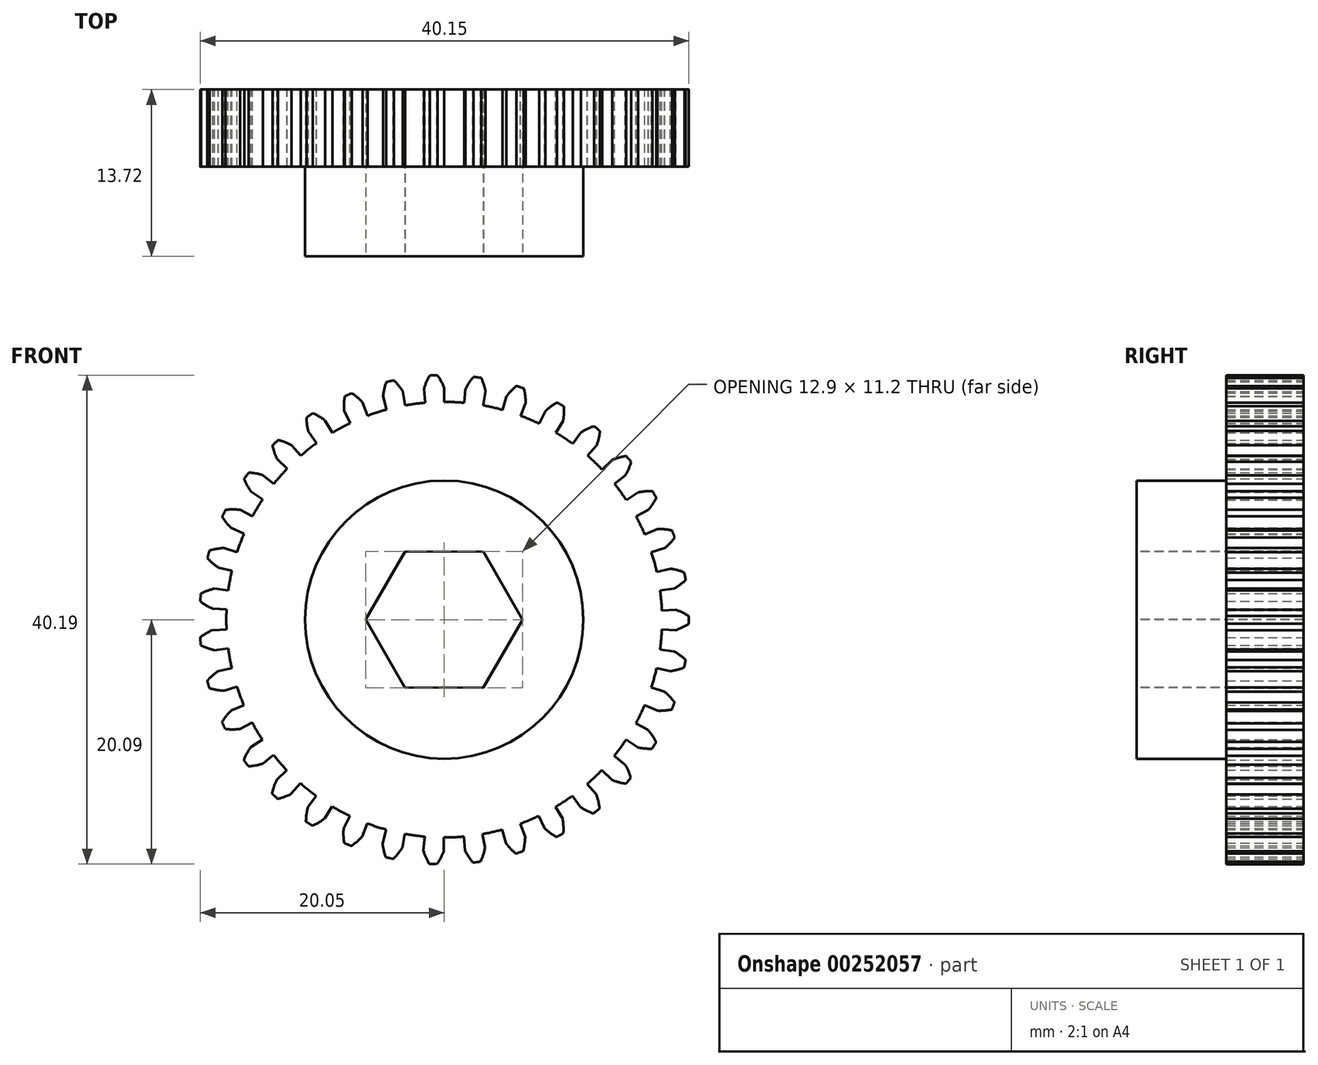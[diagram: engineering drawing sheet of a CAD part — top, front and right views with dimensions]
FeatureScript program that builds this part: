
annotation { "Feature Type Name" : "Feature", "Feature Type Description" : "" }
export const myFeature = defineFeature(function(context is Context, id is Id, definition is map)
    precondition{}
    {
        {
            var Q0;
            Q0=qCreatedBy(makeId("Front.planeOp"),FACE);
            var sketch = newSketch(context, id + "F0", { "sketchPlane" : qUnion([Q0])});
            skArc(sketch, "E0", {"start": v(-0.56, 20.1) * mm, "mid": v(-0.72, 20.1) * mm, "end": v(-0.88, 20.08) * mm});
            skLineSegment(sketch, "E1", {"start": v(0, 17.9) * mm, "end": v(0, 19.05) * mm});
            skArc(sketch, "E2", {"start": v(-1.56, 17.83) * mm, "mid": v(-2.38, 17.74) * mm, "end": v(-3.2, 17.61) * mm});
            skArc(sketch, "E3.trimOffspring", {"start": v(0, 19.05) * mm, "mid": v(-0.25, 19.6) * mm, "end": v(-0.56, 20.1) * mm});
            skPoint(sketch, "E4.orphan", {"position": v(0, 32.14) * mm});
            skPoint(sketch, "E5.orphan", {"position": v(-2.81, 32.14) * mm});
            skArc(sketch, "E6.MirrorCS", {"start": v(-1.2, 20.07) * mm, "mid": v(-1.03, 20.08) * mm, "end": v(-0.88, 20.08) * mm});
            skArc(sketch, "E7.MirrorCS", {"start": v(-1.66, 18.98) * mm, "mid": v(-1.46, 19.54) * mm, "end": v(-1.2, 20.07) * mm});
            skLineSegment(sketch, "E8.MirrorCS", {"start": v(-1.56, 17.83) * mm, "end": v(-1.66, 18.98) * mm});
            skPoint(sketch, "E9.orphan", {"position": v(-1.4, 32.14) * mm});
            skArc(sketch, "E10.1.0", {"start": v(-5.02, 18.38) * mm, "mid": v(-4.93, 18.96) * mm, "end": v(-4.76, 19.53) * mm});
            skArc(sketch, "E10.1.1", {"start": v(-4.76, 19.53) * mm, "mid": v(-4.6, 19.57) * mm, "end": v(-4.45, 19.6) * mm});
            skArc(sketch, "E10.1.2", {"start": v(-4.14, 19.67) * mm, "mid": v(-4.3, 19.64) * mm, "end": v(-4.45, 19.6) * mm});
            skArc(sketch, "E10.1.3", {"start": v(-3.4, 18.74) * mm, "mid": v(-3.74, 19.23) * mm, "end": v(-4.14, 19.67) * mm});
            skLineSegment(sketch, "E10.1.4", {"start": v(-3.2, 17.61) * mm, "end": v(-3.4, 18.74) * mm});
            skLineSegment(sketch, "E10.1.5", {"start": v(-4.72, 17.27) * mm, "end": v(-5.02, 18.38) * mm});
            skArc(sketch, "E10.2.0", {"start": v(-8.22, 17.18) * mm, "mid": v(-8.23, 17.78) * mm, "end": v(-8.17, 18.37) * mm});
            skArc(sketch, "E10.2.1", {"start": v(-8.17, 18.37) * mm, "mid": v(-8.02, 18.43) * mm, "end": v(-7.88, 18.5) * mm});
            skArc(sketch, "E10.2.2", {"start": v(-7.59, 18.62) * mm, "mid": v(-7.73, 18.56) * mm, "end": v(-7.88, 18.5) * mm});
            skArc(sketch, "E10.2.3", {"start": v(-6.7, 17.84) * mm, "mid": v(-7.12, 18.25) * mm, "end": v(-7.59, 18.62) * mm});
            skLineSegment(sketch, "E10.2.4", {"start": v(-6.3, 16.76) * mm, "end": v(-6.7, 17.84) * mm});
            skLineSegment(sketch, "E10.2.5", {"start": v(-7.73, 16.15) * mm, "end": v(-8.22, 17.18) * mm});
            skArc(sketch, "E10.3.0", {"start": v(-11.16, 15.44) * mm, "mid": v(-11.27, 16.02) * mm, "end": v(-11.32, 16.62) * mm});
            skArc(sketch, "E10.3.1", {"start": v(-11.32, 16.62) * mm, "mid": v(-11.19, 16.7) * mm, "end": v(-11.05, 16.8) * mm});
            skArc(sketch, "E10.3.2", {"start": v(-10.79, 16.96) * mm, "mid": v(-10.92, 16.88) * mm, "end": v(-11.05, 16.8) * mm});
            skArc(sketch, "E10.3.3", {"start": v(-9.77, 16.35) * mm, "mid": v(-10.26, 16.7) * mm, "end": v(-10.79, 16.96) * mm});
            skLineSegment(sketch, "E10.3.4", {"start": v(-9.18, 15.37) * mm, "end": v(-9.77, 16.35) * mm});
            skLineSegment(sketch, "E10.3.5", {"start": v(-10.49, 14.5) * mm, "end": v(-11.16, 15.44) * mm});
            skArc(sketch, "E10.4.0", {"start": v(-13.74, 13.2) * mm, "mid": v(-13.95, 13.75) * mm, "end": v(-14.1, 14.33) * mm});
            skArc(sketch, "E10.4.1", {"start": v(-14.1, 14.33) * mm, "mid": v(-13.99, 14.44) * mm, "end": v(-13.88, 14.55) * mm});
            skArc(sketch, "E10.4.2", {"start": v(-13.64, 14.76) * mm, "mid": v(-13.76, 14.66) * mm, "end": v(-13.88, 14.55) * mm});
            skArc(sketch, "E10.4.3", {"start": v(-12.53, 14.35) * mm, "mid": v(-13.08, 14.6) * mm, "end": v(-13.64, 14.76) * mm});
            skLineSegment(sketch, "E10.4.4", {"start": v(-11.78, 13.48) * mm, "end": v(-12.53, 14.35) * mm});
            skLineSegment(sketch, "E10.4.5", {"start": v(-12.9, 12.4) * mm, "end": v(-13.74, 13.2) * mm});
            skArc(sketch, "E10.5.0", {"start": v(-15.87, 10.53) * mm, "mid": v(-16.19, 11.04) * mm, "end": v(-16.43, 11.58) * mm});
            skArc(sketch, "E10.5.1", {"start": v(-16.43, 11.58) * mm, "mid": v(-16.34, 11.7) * mm, "end": v(-16.25, 11.84) * mm});
            skArc(sketch, "E10.5.2", {"start": v(-16.06, 12.1) * mm, "mid": v(-16.16, 11.96) * mm, "end": v(-16.25, 11.84) * mm});
            skArc(sketch, "E10.5.3", {"start": v(-14.9, 11.88) * mm, "mid": v(-15.47, 12.02) * mm, "end": v(-16.06, 12.1) * mm});
            skLineSegment(sketch, "E10.5.4", {"start": v(-14, 11.16) * mm, "end": v(-14.9, 11.88) * mm});
            skLineSegment(sketch, "E10.5.5", {"start": v(-14.92, 9.9) * mm, "end": v(-15.87, 10.53) * mm});
            skArc(sketch, "E10.6.0", {"start": v(-17.5, 7.53) * mm, "mid": v(-17.9, 7.97) * mm, "end": v(-18.24, 8.46) * mm});
            skArc(sketch, "E10.6.1", {"start": v(-18.24, 8.46) * mm, "mid": v(-18.17, 8.6) * mm, "end": v(-18.1, 8.75) * mm});
            skArc(sketch, "E10.6.2", {"start": v(-17.96, 9.03) * mm, "mid": v(-18.03, 8.89) * mm, "end": v(-18.1, 8.75) * mm});
            skArc(sketch, "E10.6.3", {"start": v(-16.78, 9.03) * mm, "mid": v(-17.37, 9.07) * mm, "end": v(-17.96, 9.03) * mm});
            skLineSegment(sketch, "E10.6.4", {"start": v(-15.76, 8.48) * mm, "end": v(-16.78, 9.03) * mm});
            skLineSegment(sketch, "E10.6.5", {"start": v(-16.44, 7.08) * mm, "end": v(-17.5, 7.53) * mm});
            skArc(sketch, "E10.7.0", {"start": v(-18.56, 4.29) * mm, "mid": v(-19.03, 4.65) * mm, "end": v(-19.46, 5.07) * mm});
            skArc(sketch, "E10.7.1", {"start": v(-19.46, 5.07) * mm, "mid": v(-19.41, 5.22) * mm, "end": v(-19.37, 5.37) * mm});
            skArc(sketch, "E10.7.2", {"start": v(-19.29, 5.68) * mm, "mid": v(-19.33, 5.52) * mm, "end": v(-19.37, 5.37) * mm});
            skArc(sketch, "E10.7.3", {"start": v(-18.12, 5.89) * mm, "mid": v(-18.7, 5.82) * mm, "end": v(-19.29, 5.68) * mm});
            skLineSegment(sketch, "E10.7.4", {"start": v(-17.03, 5.53) * mm, "end": v(-18.12, 5.89) * mm});
            skLineSegment(sketch, "E10.7.5", {"start": v(-17.44, 4.03) * mm, "end": v(-18.56, 4.29) * mm});
            skArc(sketch, "E10.8.0", {"start": v(-19.03, 0.9) * mm, "mid": v(-19.56, 1.18) * mm, "end": v(-20.05, 1.51) * mm});
            skArc(sketch, "E10.8.1", {"start": v(-20.05, 1.51) * mm, "mid": v(-20.03, 1.67) * mm, "end": v(-20.02, 1.83) * mm});
            skArc(sketch, "E10.8.2", {"start": v(-19.99, 2.14) * mm, "mid": v(-20, 1.98) * mm, "end": v(-20.02, 1.83) * mm});
            skArc(sketch, "E10.8.3", {"start": v(-18.88, 2.56) * mm, "mid": v(-19.45, 2.38) * mm, "end": v(-19.99, 2.14) * mm});
            skLineSegment(sketch, "E10.8.4", {"start": v(-17.74, 2.4) * mm, "end": v(-18.88, 2.56) * mm});
            skLineSegment(sketch, "E10.8.5", {"start": v(-17.88, 0.85) * mm, "end": v(-19.03, 0.9) * mm});
            skArc(sketch, "E10.9.0", {"start": v(-18.88, -2.51) * mm, "mid": v(-19.45, -2.34) * mm, "end": v(-20, -2.1) * mm});
            skArc(sketch, "E10.9.1", {"start": v(-20, -2.1) * mm, "mid": v(-20.01, -1.93) * mm, "end": v(-20.03, -1.78) * mm});
            skArc(sketch, "E10.9.2", {"start": v(-20.05, -1.46) * mm, "mid": v(-20.04, -1.62) * mm, "end": v(-20.03, -1.78) * mm});
            skArc(sketch, "E10.9.3", {"start": v(-19.03, -0.85) * mm, "mid": v(-19.56, -1.13) * mm, "end": v(-20.05, -1.46) * mm});
            skLineSegment(sketch, "E10.9.4", {"start": v(-17.88, -0.8) * mm, "end": v(-19.03, -0.85) * mm});
            skLineSegment(sketch, "E10.9.5", {"start": v(-17.75, -2.36) * mm, "end": v(-18.88, -2.51) * mm});
            skArc(sketch, "E10.10.0", {"start": v(-18.13, -5.84) * mm, "mid": v(-18.72, -5.77) * mm, "end": v(-19.3, -5.63) * mm});
            skArc(sketch, "E10.10.1", {"start": v(-19.3, -5.63) * mm, "mid": v(-19.34, -5.48) * mm, "end": v(-19.39, -5.32) * mm});
            skArc(sketch, "E10.10.2", {"start": v(-19.47, -5.02) * mm, "mid": v(-19.43, -5.17) * mm, "end": v(-19.39, -5.32) * mm});
            skArc(sketch, "E10.10.3", {"start": v(-18.57, -4.24) * mm, "mid": v(-19.04, -4.6) * mm, "end": v(-19.47, -5.02) * mm});
            skLineSegment(sketch, "E10.10.4", {"start": v(-17.45, -3.98) * mm, "end": v(-18.57, -4.24) * mm});
            skLineSegment(sketch, "E10.10.5", {"start": v(-17.04, -5.49) * mm, "end": v(-18.13, -5.84) * mm});
            skArc(sketch, "E10.11.0", {"start": v(-16.8, -8.99) * mm, "mid": v(-17.4, -9.02) * mm, "end": v(-17.98, -8.98) * mm});
            skArc(sketch, "E10.11.1", {"start": v(-17.98, -8.98) * mm, "mid": v(-18.06, -8.84) * mm, "end": v(-18.12, -8.7) * mm});
            skArc(sketch, "E10.11.2", {"start": v(-18.26, -8.41) * mm, "mid": v(-18.2, -8.56) * mm, "end": v(-18.12, -8.7) * mm});
            skArc(sketch, "E10.11.3", {"start": v(-17.52, -7.49) * mm, "mid": v(-17.92, -7.93) * mm, "end": v(-18.26, -8.41) * mm});
            skLineSegment(sketch, "E10.11.4", {"start": v(-16.46, -7.04) * mm, "end": v(-17.52, -7.49) * mm});
            skLineSegment(sketch, "E10.11.5", {"start": v(-15.78, -8.44) * mm, "end": v(-16.8, -8.99) * mm});
            skArc(sketch, "E10.12.0", {"start": v(-14.92, -11.84) * mm, "mid": v(-15.5, -11.98) * mm, "end": v(-16.1, -12.05) * mm});
            skArc(sketch, "E10.12.1", {"start": v(-16.1, -12.05) * mm, "mid": v(-16.19, -11.92) * mm, "end": v(-16.28, -11.8) * mm});
            skArc(sketch, "E10.12.2", {"start": v(-16.46, -11.54) * mm, "mid": v(-16.37, -11.67) * mm, "end": v(-16.28, -11.8) * mm});
            skArc(sketch, "E10.12.3", {"start": v(-15.9, -10.5) * mm, "mid": v(-16.21, -11) * mm, "end": v(-16.46, -11.54) * mm});
            skLineSegment(sketch, "E10.12.4", {"start": v(-14.94, -9.86) * mm, "end": v(-15.9, -10.5) * mm});
            skLineSegment(sketch, "E10.12.5", {"start": v(-14.02, -11.13) * mm, "end": v(-14.92, -11.84) * mm});
            skArc(sketch, "E10.13.0", {"start": v(-12.57, -14.31) * mm, "mid": v(-13.11, -14.56) * mm, "end": v(-13.68, -14.73) * mm});
            skArc(sketch, "E10.13.1", {"start": v(-13.68, -14.73) * mm, "mid": v(-13.8, -14.62) * mm, "end": v(-13.91, -14.51) * mm});
            skArc(sketch, "E10.13.2", {"start": v(-14.14, -14.3) * mm, "mid": v(-14.03, -14.4) * mm, "end": v(-13.91, -14.51) * mm});
            skArc(sketch, "E10.13.3", {"start": v(-13.77, -13.16) * mm, "mid": v(-13.99, -13.72) * mm, "end": v(-14.14, -14.3) * mm});
            skLineSegment(sketch, "E10.13.4", {"start": v(-12.94, -12.37) * mm, "end": v(-13.77, -13.16) * mm});
            skLineSegment(sketch, "E10.13.5", {"start": v(-11.81, -13.45) * mm, "end": v(-12.57, -14.31) * mm});
            skArc(sketch, "E10.14.0", {"start": v(-9.81, -16.33) * mm, "mid": v(-10.3, -16.66) * mm, "end": v(-10.83, -16.94) * mm});
            skArc(sketch, "E10.14.1", {"start": v(-10.83, -16.94) * mm, "mid": v(-10.96, -16.85) * mm, "end": v(-11.1, -16.76) * mm});
            skArc(sketch, "E10.14.2", {"start": v(-11.36, -16.59) * mm, "mid": v(-11.23, -16.68) * mm, "end": v(-11.1, -16.76) * mm});
            skArc(sketch, "E10.14.3", {"start": v(-11.2, -15.41) * mm, "mid": v(-11.31, -16) * mm, "end": v(-11.36, -16.59) * mm});
            skLineSegment(sketch, "E10.14.4", {"start": v(-10.52, -14.48) * mm, "end": v(-11.2, -15.41) * mm});
            skLineSegment(sketch, "E10.14.5", {"start": v(-9.22, -15.34) * mm, "end": v(-9.81, -16.33) * mm});
            skArc(sketch, "E10.15.0", {"start": v(-6.74, -17.82) * mm, "mid": v(-7.16, -18.24) * mm, "end": v(-7.63, -18.6) * mm});
            skArc(sketch, "E10.15.1", {"start": v(-7.63, -18.6) * mm, "mid": v(-7.78, -18.54) * mm, "end": v(-7.92, -18.48) * mm});
            skArc(sketch, "E10.15.2", {"start": v(-8.21, -18.35) * mm, "mid": v(-8.07, -18.41) * mm, "end": v(-7.92, -18.48) * mm});
            skArc(sketch, "E10.15.3", {"start": v(-8.27, -17.16) * mm, "mid": v(-8.28, -17.76) * mm, "end": v(-8.21, -18.35) * mm});
            skLineSegment(sketch, "E10.15.4", {"start": v(-7.77, -16.13) * mm, "end": v(-8.27, -17.16) * mm});
            skLineSegment(sketch, "E10.15.5", {"start": v(-6.33, -16.74) * mm, "end": v(-6.74, -17.82) * mm});
            skArc(sketch, "E10.16.0", {"start": v(-3.45, -18.74) * mm, "mid": v(-3.79, -19.22) * mm, "end": v(-4.19, -19.66) * mm});
            skArc(sketch, "E10.16.1", {"start": v(-4.19, -19.66) * mm, "mid": v(-4.34, -19.63) * mm, "end": v(-4.5, -19.6) * mm});
            skArc(sketch, "E10.16.2", {"start": v(-4.8, -19.52) * mm, "mid": v(-4.65, -19.56) * mm, "end": v(-4.5, -19.6) * mm});
            skArc(sketch, "E10.16.3", {"start": v(-5.07, -18.36) * mm, "mid": v(-4.97, -18.95) * mm, "end": v(-4.8, -19.52) * mm});
            skLineSegment(sketch, "E10.16.4", {"start": v(-4.76, -17.26) * mm, "end": v(-5.07, -18.36) * mm});
            skLineSegment(sketch, "E10.16.5", {"start": v(-3.24, -17.6) * mm, "end": v(-3.45, -18.74) * mm});
            skArc(sketch, "E10.17.0", {"start": v(-0.05, -19.05) * mm, "mid": v(-0.3, -19.6) * mm, "end": v(-0.61, -20.1) * mm});
            skArc(sketch, "E10.17.1", {"start": v(-0.61, -20.1) * mm, "mid": v(-0.77, -20.09) * mm, "end": v(-0.93, -20.08) * mm});
            skArc(sketch, "E10.17.2", {"start": v(-1.24, -20.07) * mm, "mid": v(-1.08, -20.07) * mm, "end": v(-0.93, -20.08) * mm});
            skArc(sketch, "E10.17.3", {"start": v(-1.7, -18.97) * mm, "mid": v(-1.5, -19.53) * mm, "end": v(-1.24, -20.07) * mm});
            skLineSegment(sketch, "E10.17.4", {"start": v(-1.6, -17.83) * mm, "end": v(-1.7, -18.97) * mm});
            skLineSegment(sketch, "E10.17.5", {"start": v(-0.04, -17.9) * mm, "end": v(-0.05, -19.05) * mm});
            skArc(sketch, "E10.18.0", {"start": v(3.35, -18.75) * mm, "mid": v(3.2, -19.33) * mm, "end": v(2.99, -19.88) * mm});
            skArc(sketch, "E10.18.1", {"start": v(2.99, -19.88) * mm, "mid": v(2.83, -19.9) * mm, "end": v(2.67, -19.93) * mm});
            skArc(sketch, "E10.18.2", {"start": v(2.36, -19.97) * mm, "mid": v(2.52, -19.95) * mm, "end": v(2.67, -19.93) * mm});
            skArc(sketch, "E10.18.3", {"start": v(1.7, -18.97) * mm, "mid": v(2, -19.49) * mm, "end": v(2.36, -19.97) * mm});
            skLineSegment(sketch, "E10.18.4", {"start": v(1.6, -17.83) * mm, "end": v(1.7, -18.97) * mm});
            skLineSegment(sketch, "E10.18.5", {"start": v(3.15, -17.62) * mm, "end": v(3.35, -18.75) * mm});
            skArc(sketch, "E10.19.0", {"start": v(6.65, -17.85) * mm, "mid": v(6.6, -18.45) * mm, "end": v(6.49, -19.03) * mm});
            skArc(sketch, "E10.19.1", {"start": v(6.49, -19.03) * mm, "mid": v(6.34, -19.08) * mm, "end": v(6.19, -19.13) * mm});
            skArc(sketch, "E10.19.2", {"start": v(5.89, -19.22) * mm, "mid": v(6.04, -19.18) * mm, "end": v(6.19, -19.13) * mm});
            skArc(sketch, "E10.19.3", {"start": v(5.07, -18.36) * mm, "mid": v(5.45, -18.82) * mm, "end": v(5.89, -19.22) * mm});
            skLineSegment(sketch, "E10.19.4", {"start": v(4.76, -17.26) * mm, "end": v(5.07, -18.36) * mm});
            skLineSegment(sketch, "E10.19.5", {"start": v(6.25, -16.78) * mm, "end": v(6.65, -17.85) * mm});
            skArc(sketch, "E10.20.0", {"start": v(9.73, -16.38) * mm, "mid": v(9.8, -16.97) * mm, "end": v(9.78, -17.56) * mm});
            skArc(sketch, "E10.20.1", {"start": v(9.78, -17.56) * mm, "mid": v(9.64, -17.64) * mm, "end": v(9.5, -17.72) * mm});
            skArc(sketch, "E10.20.2", {"start": v(9.22, -17.86) * mm, "mid": v(9.37, -17.79) * mm, "end": v(9.5, -17.72) * mm});
            skArc(sketch, "E10.20.3", {"start": v(8.27, -17.16) * mm, "mid": v(8.72, -17.54) * mm, "end": v(9.22, -17.86) * mm});
            skLineSegment(sketch, "E10.20.4", {"start": v(7.77, -16.13) * mm, "end": v(8.27, -17.16) * mm});
            skLineSegment(sketch, "E10.20.5", {"start": v(9.14, -15.4) * mm, "end": v(9.73, -16.38) * mm});
            skArc(sketch, "E10.21.0", {"start": v(12.5, -14.38) * mm, "mid": v(12.67, -14.95) * mm, "end": v(12.76, -15.53) * mm});
            skArc(sketch, "E10.21.1", {"start": v(12.76, -15.53) * mm, "mid": v(12.64, -15.63) * mm, "end": v(12.52, -15.73) * mm});
            skArc(sketch, "E10.21.2", {"start": v(12.27, -15.93) * mm, "mid": v(12.4, -15.83) * mm, "end": v(12.52, -15.73) * mm});
            skArc(sketch, "E10.21.3", {"start": v(11.2, -15.41) * mm, "mid": v(11.72, -15.7) * mm, "end": v(12.27, -15.93) * mm});
            skLineSegment(sketch, "E10.21.4", {"start": v(10.52, -14.48) * mm, "end": v(11.2, -15.41) * mm});
            skLineSegment(sketch, "E10.21.5", {"start": v(11.74, -13.51) * mm, "end": v(12.5, -14.38) * mm});
            skArc(sketch, "E10.22.0", {"start": v(14.86, -11.91) * mm, "mid": v(15.13, -12.45) * mm, "end": v(15.33, -13) * mm});
            skArc(sketch, "E10.22.1", {"start": v(15.33, -13) * mm, "mid": v(15.23, -13.13) * mm, "end": v(15.12, -13.25) * mm});
            skArc(sketch, "E10.22.2", {"start": v(14.91, -13.48) * mm, "mid": v(15.02, -13.36) * mm, "end": v(15.12, -13.25) * mm});
            skArc(sketch, "E10.22.3", {"start": v(13.77, -13.16) * mm, "mid": v(14.33, -13.36) * mm, "end": v(14.91, -13.48) * mm});
            skLineSegment(sketch, "E10.22.4", {"start": v(12.94, -12.37) * mm, "end": v(13.77, -13.16) * mm});
            skLineSegment(sketch, "E10.22.5", {"start": v(13.97, -11.2) * mm, "end": v(14.86, -11.91) * mm});
            skArc(sketch, "E10.23.0", {"start": v(16.75, -9.07) * mm, "mid": v(17.11, -9.54) * mm, "end": v(17.4, -10.06) * mm});
            skArc(sketch, "E10.23.1", {"start": v(17.4, -10.06) * mm, "mid": v(17.33, -10.2) * mm, "end": v(17.25, -10.33) * mm});
            skArc(sketch, "E10.23.2", {"start": v(17.08, -10.6) * mm, "mid": v(17.16, -10.47) * mm, "end": v(17.25, -10.33) * mm});
            skArc(sketch, "E10.23.3", {"start": v(15.9, -10.5) * mm, "mid": v(16.49, -10.59) * mm, "end": v(17.08, -10.6) * mm});
            skLineSegment(sketch, "E10.23.4", {"start": v(14.94, -9.86) * mm, "end": v(15.9, -10.5) * mm});
            skLineSegment(sketch, "E10.23.5", {"start": v(15.74, -8.52) * mm, "end": v(16.75, -9.07) * mm});
            skArc(sketch, "E10.24.0", {"start": v(18.1, -5.93) * mm, "mid": v(18.54, -6.34) * mm, "end": v(18.92, -6.8) * mm});
            skArc(sketch, "E10.24.1", {"start": v(18.92, -6.8) * mm, "mid": v(18.87, -6.94) * mm, "end": v(18.81, -7.09) * mm});
            skArc(sketch, "E10.24.2", {"start": v(18.7, -7.38) * mm, "mid": v(18.76, -7.24) * mm, "end": v(18.81, -7.09) * mm});
            skArc(sketch, "E10.24.3", {"start": v(17.52, -7.49) * mm, "mid": v(18.11, -7.47) * mm, "end": v(18.7, -7.38) * mm});
            skLineSegment(sketch, "E10.24.4", {"start": v(16.46, -7.04) * mm, "end": v(17.52, -7.49) * mm});
            skLineSegment(sketch, "E10.24.5", {"start": v(17.01, -5.57) * mm, "end": v(18.1, -5.93) * mm});
            skArc(sketch, "E10.25.0", {"start": v(18.87, -2.6) * mm, "mid": v(19.37, -2.92) * mm, "end": v(19.83, -3.3) * mm});
            skArc(sketch, "E10.25.1", {"start": v(19.83, -3.3) * mm, "mid": v(19.8, -3.46) * mm, "end": v(19.78, -3.61) * mm});
            skArc(sketch, "E10.25.2", {"start": v(19.72, -3.92) * mm, "mid": v(19.75, -3.77) * mm, "end": v(19.78, -3.61) * mm});
            skArc(sketch, "E10.25.3", {"start": v(18.57, -4.24) * mm, "mid": v(19.15, -4.12) * mm, "end": v(19.72, -3.92) * mm});
            skLineSegment(sketch, "E10.25.4", {"start": v(17.45, -3.98) * mm, "end": v(18.57, -4.24) * mm});
            skLineSegment(sketch, "E10.25.5", {"start": v(17.73, -2.45) * mm, "end": v(18.87, -2.6) * mm});
            skArc(sketch, "E10.26.0", {"start": v(19.03, 0.8) * mm, "mid": v(19.58, 0.58) * mm, "end": v(20.1, 0.3) * mm});
            skArc(sketch, "E10.26.1", {"start": v(20.1, 0.3) * mm, "mid": v(20.1, 0.13) * mm, "end": v(20.1, -0.03) * mm});
            skArc(sketch, "E10.26.2", {"start": v(20.1, -0.34) * mm, "mid": v(20.1, -0.18) * mm, "end": v(20.1, -0.03) * mm});
            skArc(sketch, "E10.26.3", {"start": v(19.03, -0.85) * mm, "mid": v(19.58, -0.63) * mm, "end": v(20.1, -0.34) * mm});
            skLineSegment(sketch, "E10.26.4", {"start": v(17.88, -0.8) * mm, "end": v(19.03, -0.85) * mm});
            skLineSegment(sketch, "E10.26.5", {"start": v(17.89, 0.76) * mm, "end": v(19.03, 0.8) * mm});
            skArc(sketch, "E10.27.0", {"start": v(18.58, 4.2) * mm, "mid": v(19.16, 4.07) * mm, "end": v(19.73, 3.88) * mm});
            skArc(sketch, "E10.27.1", {"start": v(19.73, 3.88) * mm, "mid": v(19.76, 3.72) * mm, "end": v(19.79, 3.57) * mm});
            skArc(sketch, "E10.27.2", {"start": v(19.84, 3.25) * mm, "mid": v(19.81, 3.4) * mm, "end": v(19.79, 3.57) * mm});
            skArc(sketch, "E10.27.3", {"start": v(18.88, 2.56) * mm, "mid": v(19.38, 2.88) * mm, "end": v(19.84, 3.25) * mm});
            skLineSegment(sketch, "E10.27.4", {"start": v(17.74, 2.4) * mm, "end": v(18.88, 2.56) * mm});
            skLineSegment(sketch, "E10.27.5", {"start": v(17.46, 3.94) * mm, "end": v(18.58, 4.2) * mm});
            skArc(sketch, "E10.28.0", {"start": v(17.54, 7.44) * mm, "mid": v(18.13, 7.43) * mm, "end": v(18.72, 7.34) * mm});
            skArc(sketch, "E10.28.1", {"start": v(18.72, 7.34) * mm, "mid": v(18.77, 7.19) * mm, "end": v(18.83, 7.04) * mm});
            skArc(sketch, "E10.28.2", {"start": v(18.94, 6.74) * mm, "mid": v(18.89, 6.9) * mm, "end": v(18.83, 7.04) * mm});
            skArc(sketch, "E10.28.3", {"start": v(18.12, 5.89) * mm, "mid": v(18.56, 6.29) * mm, "end": v(18.94, 6.74) * mm});
            skLineSegment(sketch, "E10.28.4", {"start": v(17.03, 5.53) * mm, "end": v(18.12, 5.89) * mm});
            skLineSegment(sketch, "E10.28.5", {"start": v(16.48, 7) * mm, "end": v(17.54, 7.44) * mm});
            skArc(sketch, "E10.29.0", {"start": v(15.92, 10.45) * mm, "mid": v(16.51, 10.54) * mm, "end": v(17.1, 10.56) * mm});
            skArc(sketch, "E10.29.1", {"start": v(17.1, 10.56) * mm, "mid": v(17.19, 10.43) * mm, "end": v(17.27, 10.29) * mm});
            skArc(sketch, "E10.29.2", {"start": v(17.43, 10.02) * mm, "mid": v(17.35, 10.15) * mm, "end": v(17.27, 10.29) * mm});
            skArc(sketch, "E10.29.3", {"start": v(16.78, 9.03) * mm, "mid": v(17.13, 9.5) * mm, "end": v(17.43, 10.02) * mm});
            skLineSegment(sketch, "E10.29.4", {"start": v(15.76, 8.48) * mm, "end": v(16.78, 9.03) * mm});
            skLineSegment(sketch, "E10.29.5", {"start": v(14.96, 9.82) * mm, "end": v(15.92, 10.45) * mm});
            skArc(sketch, "E10.30.0", {"start": v(13.8, 13.13) * mm, "mid": v(14.36, 13.32) * mm, "end": v(14.95, 13.45) * mm});
            skArc(sketch, "E10.30.1", {"start": v(14.95, 13.45) * mm, "mid": v(15.05, 13.33) * mm, "end": v(15.16, 13.2) * mm});
            skArc(sketch, "E10.30.2", {"start": v(15.36, 12.97) * mm, "mid": v(15.26, 13.09) * mm, "end": v(15.16, 13.2) * mm});
            skArc(sketch, "E10.30.3", {"start": v(14.9, 11.88) * mm, "mid": v(15.16, 12.4) * mm, "end": v(15.36, 12.97) * mm});
            skLineSegment(sketch, "E10.30.4", {"start": v(14, 11.16) * mm, "end": v(14.9, 11.88) * mm});
            skLineSegment(sketch, "E10.30.5", {"start": v(12.97, 12.34) * mm, "end": v(13.8, 13.13) * mm});
            skArc(sketch, "E10.31.0", {"start": v(11.24, 15.38) * mm, "mid": v(11.75, 15.67) * mm, "end": v(12.3, 15.9) * mm});
            skArc(sketch, "E10.31.1", {"start": v(12.3, 15.9) * mm, "mid": v(12.43, 15.8) * mm, "end": v(12.55, 15.7) * mm});
            skArc(sketch, "E10.31.2", {"start": v(12.8, 15.5) * mm, "mid": v(12.68, 15.6) * mm, "end": v(12.55, 15.7) * mm});
            skArc(sketch, "E10.31.3", {"start": v(12.53, 14.35) * mm, "mid": v(12.7, 14.92) * mm, "end": v(12.8, 15.5) * mm});
            skLineSegment(sketch, "E10.31.4", {"start": v(11.78, 13.48) * mm, "end": v(12.53, 14.35) * mm});
            skLineSegment(sketch, "E10.31.5", {"start": v(10.56, 14.46) * mm, "end": v(11.24, 15.38) * mm});
            skArc(sketch, "E10.32.0", {"start": v(8.3, 17.14) * mm, "mid": v(8.77, 17.52) * mm, "end": v(9.27, 17.84) * mm});
            skArc(sketch, "E10.32.1", {"start": v(9.27, 17.84) * mm, "mid": v(9.4, 17.77) * mm, "end": v(9.55, 17.7) * mm});
            skArc(sketch, "E10.32.2", {"start": v(9.83, 17.54) * mm, "mid": v(9.69, 17.62) * mm, "end": v(9.55, 17.7) * mm});
            skArc(sketch, "E10.32.3", {"start": v(9.77, 16.35) * mm, "mid": v(9.84, 16.94) * mm, "end": v(9.83, 17.54) * mm});
            skLineSegment(sketch, "E10.32.4", {"start": v(9.18, 15.37) * mm, "end": v(9.77, 16.35) * mm});
            skLineSegment(sketch, "E10.32.5", {"start": v(7.8, 16.1) * mm, "end": v(8.3, 17.14) * mm});
            skArc(sketch, "E10.33.0", {"start": v(5.11, 18.35) * mm, "mid": v(5.5, 18.8) * mm, "end": v(5.93, 19.2) * mm});
            skArc(sketch, "E10.33.1", {"start": v(5.93, 19.2) * mm, "mid": v(6.09, 19.16) * mm, "end": v(6.24, 19.11) * mm});
            skArc(sketch, "E10.33.2", {"start": v(6.54, 19.01) * mm, "mid": v(6.39, 19.06) * mm, "end": v(6.24, 19.11) * mm});
            skArc(sketch, "E10.33.3", {"start": v(6.7, 17.84) * mm, "mid": v(6.65, 18.43) * mm, "end": v(6.54, 19.01) * mm});
            skLineSegment(sketch, "E10.33.4", {"start": v(6.3, 16.76) * mm, "end": v(6.7, 17.84) * mm});
            skLineSegment(sketch, "E10.33.5", {"start": v(4.8, 17.24) * mm, "end": v(5.11, 18.35) * mm});
            skArc(sketch, "E10.34.0", {"start": v(1.75, 18.97) * mm, "mid": v(2.05, 19.48) * mm, "end": v(2.4, 19.96) * mm});
            skArc(sketch, "E10.34.1", {"start": v(2.4, 19.96) * mm, "mid": v(2.57, 19.94) * mm, "end": v(2.72, 19.92) * mm});
            skArc(sketch, "E10.34.2", {"start": v(3.04, 19.87) * mm, "mid": v(2.88, 19.9) * mm, "end": v(2.72, 19.92) * mm});
            skArc(sketch, "E10.34.3", {"start": v(3.4, 18.74) * mm, "mid": v(3.25, 19.32) * mm, "end": v(3.04, 19.87) * mm});
            skLineSegment(sketch, "E10.34.4", {"start": v(3.2, 17.61) * mm, "end": v(3.4, 18.74) * mm});
            skLineSegment(sketch, "E10.34.5", {"start": v(1.65, 17.83) * mm, "end": v(1.75, 18.97) * mm});
            skArc(sketch, "E11.trimOffspring", {"start": v(1.65, 17.83) * mm, "mid": v(0.83, 17.88) * mm, "end": v(0, 17.9) * mm});
            skArc(sketch, "E12.trimOffspring", {"start": v(4.8, 17.24) * mm, "mid": v(4, 17.45) * mm, "end": v(3.2, 17.61) * mm});
            skArc(sketch, "E13.trimOffspring", {"start": v(7.8, 16.1) * mm, "mid": v(7.06, 16.45) * mm, "end": v(6.3, 16.76) * mm});
            skArc(sketch, "E14.trimOffspring", {"start": v(10.56, 14.46) * mm, "mid": v(9.88, 14.93) * mm, "end": v(9.18, 15.37) * mm});
            skArc(sketch, "E15.trimOffspring", {"start": v(12.97, 12.34) * mm, "mid": v(12.39, 12.92) * mm, "end": v(11.78, 13.48) * mm});
            skArc(sketch, "E16.trimOffspring", {"start": v(14.96, 9.82) * mm, "mid": v(14.5, 10.5) * mm, "end": v(14, 11.16) * mm});
            skArc(sketch, "E17.trimOffspring", {"start": v(16.48, 7) * mm, "mid": v(16.14, 7.75) * mm, "end": v(15.76, 8.48) * mm});
            skArc(sketch, "E18.trimOffspring", {"start": v(17.46, 3.94) * mm, "mid": v(17.26, 4.74) * mm, "end": v(17.03, 5.53) * mm});
            skArc(sketch, "E19.trimOffspring", {"start": v(17.89, 0.76) * mm, "mid": v(17.83, 1.58) * mm, "end": v(17.74, 2.4) * mm});
            skArc(sketch, "E20.trimOffspring", {"start": v(17.73, -2.45) * mm, "mid": v(17.83, -1.63) * mm, "end": v(17.88, -0.8) * mm});
            skArc(sketch, "E21.trimOffspring", {"start": v(17.01, -5.57) * mm, "mid": v(17.25, -4.78) * mm, "end": v(17.45, -3.98) * mm});
            skArc(sketch, "E22.trimOffspring", {"start": v(15.74, -8.52) * mm, "mid": v(16.12, -7.79) * mm, "end": v(16.46, -7.04) * mm});
            skArc(sketch, "E23.trimOffspring", {"start": v(13.97, -11.2) * mm, "mid": v(14.47, -10.54) * mm, "end": v(14.94, -9.86) * mm});
            skArc(sketch, "E24.trimOffspring", {"start": v(11.74, -13.51) * mm, "mid": v(12.35, -12.95) * mm, "end": v(12.94, -12.37) * mm});
            skArc(sketch, "E25.trimOffspring", {"start": v(9.14, -15.4) * mm, "mid": v(9.84, -14.95) * mm, "end": v(10.52, -14.48) * mm});
            skArc(sketch, "E26.trimOffspring", {"start": v(6.25, -16.78) * mm, "mid": v(7.02, -16.47) * mm, "end": v(7.77, -16.13) * mm});
            skArc(sketch, "E27.trimOffspring", {"start": v(3.15, -17.62) * mm, "mid": v(3.96, -17.46) * mm, "end": v(4.76, -17.26) * mm});
            skArc(sketch, "E28.trimOffspring", {"start": v(-0.04, -17.9) * mm, "mid": v(0.78, -17.88) * mm, "end": v(1.6, -17.83) * mm});
            skArc(sketch, "E29.trimOffspring", {"start": v(-3.24, -17.6) * mm, "mid": v(-2.43, -17.74) * mm, "end": v(-1.6, -17.83) * mm});
            skArc(sketch, "E30.trimOffspring", {"start": v(-6.33, -16.74) * mm, "mid": v(-5.55, -17.02) * mm, "end": v(-4.76, -17.26) * mm});
            skArc(sketch, "E31.trimOffspring", {"start": v(-9.22, -15.34) * mm, "mid": v(-8.5, -15.75) * mm, "end": v(-7.77, -16.13) * mm});
            skArc(sketch, "E32.trimOffspring", {"start": v(-11.81, -13.45) * mm, "mid": v(-11.18, -13.98) * mm, "end": v(-10.52, -14.48) * mm});
            skArc(sketch, "E33.trimOffspring", {"start": v(-14.02, -11.13) * mm, "mid": v(-13.5, -11.76) * mm, "end": v(-12.94, -12.37) * mm});
            skArc(sketch, "E34.trimOffspring", {"start": v(-15.78, -8.44) * mm, "mid": v(-15.38, -9.16) * mm, "end": v(-14.94, -9.86) * mm});
            skArc(sketch, "E35.trimOffspring", {"start": v(-17.04, -5.49) * mm, "mid": v(-16.77, -6.27) * mm, "end": v(-16.46, -7.04) * mm});
            skArc(sketch, "E36.trimOffspring", {"start": v(-17.75, -2.36) * mm, "mid": v(-17.62, -3.17) * mm, "end": v(-17.45, -3.98) * mm});
            skArc(sketch, "E37.trimOffspring", {"start": v(-17.88, 0.85) * mm, "mid": v(-17.9, 0.02) * mm, "end": v(-17.88, -0.8) * mm});
            skArc(sketch, "E38.trimOffspring", {"start": v(-17.44, 4.03) * mm, "mid": v(-17.6, 3.22) * mm, "end": v(-17.74, 2.4) * mm});
            skArc(sketch, "E39.trimOffspring", {"start": v(-16.44, 7.08) * mm, "mid": v(-16.75, 6.31) * mm, "end": v(-17.03, 5.53) * mm});
            skArc(sketch, "E40.trimOffspring", {"start": v(-14.92, 9.9) * mm, "mid": v(-15.36, 9.2) * mm, "end": v(-15.76, 8.48) * mm});
            skArc(sketch, "E41.trimOffspring", {"start": v(-12.9, 12.4) * mm, "mid": v(-13.47, 11.8) * mm, "end": v(-14, 11.16) * mm});
            skArc(sketch, "E42.trimOffspring", {"start": v(-10.49, 14.5) * mm, "mid": v(-11.14, 14) * mm, "end": v(-11.78, 13.48) * mm});
            skArc(sketch, "E43.trimOffspring", {"start": v(-7.73, 16.15) * mm, "mid": v(-8.46, 15.77) * mm, "end": v(-9.18, 15.37) * mm});
            skArc(sketch, "E44.trimOffspring", {"start": v(-4.72, 17.27) * mm, "mid": v(-5.51, 17.03) * mm, "end": v(-6.3, 16.76) * mm});
            skSolve(sketch);
        }
        {
            var Q0;
            Q0 = qSketchRegion(id + "F0", true);
            var Q1;
            Q1=makeQuery(id+"F0.imprint","IMPRINT",FACE,{"disambiguationData":[TD([[makeQuery(id+"F0.imprint","IMPRINT",EDGE,{"derivedFrom":sQuery(id+"F0.wireOp",EDGE,"E0")}),1.0]])]});
            extrude(context, id + "F1", {"entities" : qUnion([Q0, Q1]), "depth" : 6.35 * mm});
        }
        {
            var Q0;
            Q0=makeQuery(id+"F1.opExtrude","CAP_FACE",FACE,{"disambiguationData":[OSD([sQuery(id+"F0.wireOp",EDGE,"E0"),sQuery(id+"F0.wireOp",EDGE,"E1"),sQuery(id+"F0.wireOp",EDGE,"E2"),sQuery(id+"F0.wireOp",EDGE,"E3.trimOffspring"),sQuery(id+"F0.wireOp",EDGE,"E6.MirrorCS"),sQuery(id+"F0.wireOp",EDGE,"E7.MirrorCS"),sQuery(id+"F0.wireOp",EDGE,"E8.MirrorCS"),sQuery(id+"F0.wireOp",EDGE,"E10.1.0"),sQuery(id+"F0.wireOp",EDGE,"E10.1.1"),sQuery(id+"F0.wireOp",EDGE,"E10.1.2"),sQuery(id+"F0.wireOp",EDGE,"E10.1.3"),sQuery(id+"F0.wireOp",EDGE,"E10.1.4"),sQuery(id+"F0.wireOp",EDGE,"E10.1.5"),sQuery(id+"F0.wireOp",EDGE,"E10.2.0"),sQuery(id+"F0.wireOp",EDGE,"E10.2.1"),sQuery(id+"F0.wireOp",EDGE,"E10.2.2"),sQuery(id+"F0.wireOp",EDGE,"E10.2.3"),sQuery(id+"F0.wireOp",EDGE,"E10.2.4"),sQuery(id+"F0.wireOp",EDGE,"E10.2.5"),sQuery(id+"F0.wireOp",EDGE,"E10.3.0"),sQuery(id+"F0.wireOp",EDGE,"E10.3.1"),sQuery(id+"F0.wireOp",EDGE,"E10.3.2"),sQuery(id+"F0.wireOp",EDGE,"E10.3.3"),sQuery(id+"F0.wireOp",EDGE,"E10.3.4"),sQuery(id+"F0.wireOp",EDGE,"E10.3.5"),sQuery(id+"F0.wireOp",EDGE,"E10.4.0"),sQuery(id+"F0.wireOp",EDGE,"E10.4.1"),sQuery(id+"F0.wireOp",EDGE,"E10.4.2"),sQuery(id+"F0.wireOp",EDGE,"E10.4.3"),sQuery(id+"F0.wireOp",EDGE,"E10.4.4"),sQuery(id+"F0.wireOp",EDGE,"E10.4.5"),sQuery(id+"F0.wireOp",EDGE,"E10.5.0"),sQuery(id+"F0.wireOp",EDGE,"E10.5.1"),sQuery(id+"F0.wireOp",EDGE,"E10.5.2"),sQuery(id+"F0.wireOp",EDGE,"E10.5.3"),sQuery(id+"F0.wireOp",EDGE,"E10.5.4"),sQuery(id+"F0.wireOp",EDGE,"E10.5.5"),sQuery(id+"F0.wireOp",EDGE,"E10.6.0"),sQuery(id+"F0.wireOp",EDGE,"E10.6.1"),sQuery(id+"F0.wireOp",EDGE,"E10.6.2"),sQuery(id+"F0.wireOp",EDGE,"E10.6.3"),sQuery(id+"F0.wireOp",EDGE,"E10.6.4"),sQuery(id+"F0.wireOp",EDGE,"E10.6.5"),sQuery(id+"F0.wireOp",EDGE,"E10.7.0"),sQuery(id+"F0.wireOp",EDGE,"E10.7.1"),sQuery(id+"F0.wireOp",EDGE,"E10.7.2"),sQuery(id+"F0.wireOp",EDGE,"E10.7.3"),sQuery(id+"F0.wireOp",EDGE,"E10.7.4"),sQuery(id+"F0.wireOp",EDGE,"E10.7.5"),sQuery(id+"F0.wireOp",EDGE,"E10.8.0"),sQuery(id+"F0.wireOp",EDGE,"E10.8.1"),sQuery(id+"F0.wireOp",EDGE,"E10.8.2"),sQuery(id+"F0.wireOp",EDGE,"E10.8.3"),sQuery(id+"F0.wireOp",EDGE,"E10.8.4"),sQuery(id+"F0.wireOp",EDGE,"E10.8.5"),sQuery(id+"F0.wireOp",EDGE,"E10.9.0"),sQuery(id+"F0.wireOp",EDGE,"E10.9.1"),sQuery(id+"F0.wireOp",EDGE,"E10.9.2"),sQuery(id+"F0.wireOp",EDGE,"E10.9.3"),sQuery(id+"F0.wireOp",EDGE,"E10.9.4"),sQuery(id+"F0.wireOp",EDGE,"E10.9.5"),sQuery(id+"F0.wireOp",EDGE,"E10.10.0"),sQuery(id+"F0.wireOp",EDGE,"E10.10.1"),sQuery(id+"F0.wireOp",EDGE,"E10.10.2"),sQuery(id+"F0.wireOp",EDGE,"E10.10.3"),sQuery(id+"F0.wireOp",EDGE,"E10.10.4"),sQuery(id+"F0.wireOp",EDGE,"E10.10.5"),sQuery(id+"F0.wireOp",EDGE,"E10.11.0"),sQuery(id+"F0.wireOp",EDGE,"E10.11.1"),sQuery(id+"F0.wireOp",EDGE,"E10.11.2"),sQuery(id+"F0.wireOp",EDGE,"E10.11.3"),sQuery(id+"F0.wireOp",EDGE,"E10.11.4"),sQuery(id+"F0.wireOp",EDGE,"E10.11.5"),sQuery(id+"F0.wireOp",EDGE,"E10.12.0"),sQuery(id+"F0.wireOp",EDGE,"E10.12.1"),sQuery(id+"F0.wireOp",EDGE,"E10.12.2"),sQuery(id+"F0.wireOp",EDGE,"E10.12.3"),sQuery(id+"F0.wireOp",EDGE,"E10.12.4"),sQuery(id+"F0.wireOp",EDGE,"E10.12.5"),sQuery(id+"F0.wireOp",EDGE,"E10.13.0"),sQuery(id+"F0.wireOp",EDGE,"E10.13.1"),sQuery(id+"F0.wireOp",EDGE,"E10.13.2"),sQuery(id+"F0.wireOp",EDGE,"E10.13.3"),sQuery(id+"F0.wireOp",EDGE,"E10.13.4"),sQuery(id+"F0.wireOp",EDGE,"E10.13.5"),sQuery(id+"F0.wireOp",EDGE,"E10.14.0"),sQuery(id+"F0.wireOp",EDGE,"E10.14.1"),sQuery(id+"F0.wireOp",EDGE,"E10.14.2"),sQuery(id+"F0.wireOp",EDGE,"E10.14.3"),sQuery(id+"F0.wireOp",EDGE,"E10.14.4"),sQuery(id+"F0.wireOp",EDGE,"E10.14.5"),sQuery(id+"F0.wireOp",EDGE,"E10.15.0"),sQuery(id+"F0.wireOp",EDGE,"E10.15.1"),sQuery(id+"F0.wireOp",EDGE,"E10.15.2"),sQuery(id+"F0.wireOp",EDGE,"E10.15.3"),sQuery(id+"F0.wireOp",EDGE,"E10.15.4"),sQuery(id+"F0.wireOp",EDGE,"E10.15.5"),sQuery(id+"F0.wireOp",EDGE,"E10.16.0"),sQuery(id+"F0.wireOp",EDGE,"E10.16.1"),sQuery(id+"F0.wireOp",EDGE,"E10.16.2"),sQuery(id+"F0.wireOp",EDGE,"E10.16.3"),sQuery(id+"F0.wireOp",EDGE,"E10.16.4"),sQuery(id+"F0.wireOp",EDGE,"E10.16.5"),sQuery(id+"F0.wireOp",EDGE,"E10.17.0"),sQuery(id+"F0.wireOp",EDGE,"E10.17.1"),sQuery(id+"F0.wireOp",EDGE,"E10.17.2"),sQuery(id+"F0.wireOp",EDGE,"E10.17.3"),sQuery(id+"F0.wireOp",EDGE,"E10.17.4"),sQuery(id+"F0.wireOp",EDGE,"E10.17.5"),sQuery(id+"F0.wireOp",EDGE,"E10.18.0"),sQuery(id+"F0.wireOp",EDGE,"E10.18.1"),sQuery(id+"F0.wireOp",EDGE,"E10.18.2"),sQuery(id+"F0.wireOp",EDGE,"E10.18.3"),sQuery(id+"F0.wireOp",EDGE,"E10.18.4"),sQuery(id+"F0.wireOp",EDGE,"E10.18.5"),sQuery(id+"F0.wireOp",EDGE,"E10.19.0"),sQuery(id+"F0.wireOp",EDGE,"E10.19.1"),sQuery(id+"F0.wireOp",EDGE,"E10.19.2"),sQuery(id+"F0.wireOp",EDGE,"E10.19.3"),sQuery(id+"F0.wireOp",EDGE,"E10.19.4"),sQuery(id+"F0.wireOp",EDGE,"E10.19.5"),sQuery(id+"F0.wireOp",EDGE,"E10.20.0"),sQuery(id+"F0.wireOp",EDGE,"E10.20.1"),sQuery(id+"F0.wireOp",EDGE,"E10.20.2"),sQuery(id+"F0.wireOp",EDGE,"E10.20.3"),sQuery(id+"F0.wireOp",EDGE,"E10.20.4"),sQuery(id+"F0.wireOp",EDGE,"E10.20.5"),sQuery(id+"F0.wireOp",EDGE,"E10.21.0"),sQuery(id+"F0.wireOp",EDGE,"E10.21.1"),sQuery(id+"F0.wireOp",EDGE,"E10.21.2"),sQuery(id+"F0.wireOp",EDGE,"E10.21.3"),sQuery(id+"F0.wireOp",EDGE,"E10.21.4"),sQuery(id+"F0.wireOp",EDGE,"E10.21.5"),sQuery(id+"F0.wireOp",EDGE,"E10.22.0"),sQuery(id+"F0.wireOp",EDGE,"E10.22.1"),sQuery(id+"F0.wireOp",EDGE,"E10.22.2"),sQuery(id+"F0.wireOp",EDGE,"E10.22.3"),sQuery(id+"F0.wireOp",EDGE,"E10.22.4"),sQuery(id+"F0.wireOp",EDGE,"E10.22.5"),sQuery(id+"F0.wireOp",EDGE,"E10.23.0"),sQuery(id+"F0.wireOp",EDGE,"E10.23.1"),sQuery(id+"F0.wireOp",EDGE,"E10.23.2"),sQuery(id+"F0.wireOp",EDGE,"E10.23.3"),sQuery(id+"F0.wireOp",EDGE,"E10.23.4"),sQuery(id+"F0.wireOp",EDGE,"E10.23.5"),sQuery(id+"F0.wireOp",EDGE,"E10.24.0"),sQuery(id+"F0.wireOp",EDGE,"E10.24.1"),sQuery(id+"F0.wireOp",EDGE,"E10.24.2"),sQuery(id+"F0.wireOp",EDGE,"E10.24.3"),sQuery(id+"F0.wireOp",EDGE,"E10.24.4"),sQuery(id+"F0.wireOp",EDGE,"E10.24.5"),sQuery(id+"F0.wireOp",EDGE,"E10.25.0"),sQuery(id+"F0.wireOp",EDGE,"E10.25.1"),sQuery(id+"F0.wireOp",EDGE,"E10.25.2"),sQuery(id+"F0.wireOp",EDGE,"E10.25.3"),sQuery(id+"F0.wireOp",EDGE,"E10.25.4"),sQuery(id+"F0.wireOp",EDGE,"E10.25.5"),sQuery(id+"F0.wireOp",EDGE,"E10.26.0"),sQuery(id+"F0.wireOp",EDGE,"E10.26.1"),sQuery(id+"F0.wireOp",EDGE,"E10.26.2"),sQuery(id+"F0.wireOp",EDGE,"E10.26.3"),sQuery(id+"F0.wireOp",EDGE,"E10.26.4"),sQuery(id+"F0.wireOp",EDGE,"E10.26.5"),sQuery(id+"F0.wireOp",EDGE,"E10.27.0"),sQuery(id+"F0.wireOp",EDGE,"E10.27.1"),sQuery(id+"F0.wireOp",EDGE,"E10.27.2"),sQuery(id+"F0.wireOp",EDGE,"E10.27.3"),sQuery(id+"F0.wireOp",EDGE,"E10.27.4"),sQuery(id+"F0.wireOp",EDGE,"E10.27.5"),sQuery(id+"F0.wireOp",EDGE,"E10.28.0"),sQuery(id+"F0.wireOp",EDGE,"E10.28.1"),sQuery(id+"F0.wireOp",EDGE,"E10.28.2"),sQuery(id+"F0.wireOp",EDGE,"E10.28.3"),sQuery(id+"F0.wireOp",EDGE,"E10.28.4"),sQuery(id+"F0.wireOp",EDGE,"E10.28.5"),sQuery(id+"F0.wireOp",EDGE,"E10.29.0"),sQuery(id+"F0.wireOp",EDGE,"E10.29.1"),sQuery(id+"F0.wireOp",EDGE,"E10.29.2"),sQuery(id+"F0.wireOp",EDGE,"E10.29.3"),sQuery(id+"F0.wireOp",EDGE,"E10.29.4"),sQuery(id+"F0.wireOp",EDGE,"E10.29.5"),sQuery(id+"F0.wireOp",EDGE,"E10.30.0"),sQuery(id+"F0.wireOp",EDGE,"E10.30.1"),sQuery(id+"F0.wireOp",EDGE,"E10.30.2"),sQuery(id+"F0.wireOp",EDGE,"E10.30.3"),sQuery(id+"F0.wireOp",EDGE,"E10.30.4"),sQuery(id+"F0.wireOp",EDGE,"E10.30.5"),sQuery(id+"F0.wireOp",EDGE,"E10.31.0"),sQuery(id+"F0.wireOp",EDGE,"E10.31.1"),sQuery(id+"F0.wireOp",EDGE,"E10.31.2"),sQuery(id+"F0.wireOp",EDGE,"E10.31.3"),sQuery(id+"F0.wireOp",EDGE,"E10.31.4"),sQuery(id+"F0.wireOp",EDGE,"E10.31.5"),sQuery(id+"F0.wireOp",EDGE,"E10.32.0"),sQuery(id+"F0.wireOp",EDGE,"E10.32.1"),sQuery(id+"F0.wireOp",EDGE,"E10.32.2"),sQuery(id+"F0.wireOp",EDGE,"E10.32.3"),sQuery(id+"F0.wireOp",EDGE,"E10.32.4"),sQuery(id+"F0.wireOp",EDGE,"E10.32.5"),sQuery(id+"F0.wireOp",EDGE,"E10.33.0"),sQuery(id+"F0.wireOp",EDGE,"E10.33.1"),sQuery(id+"F0.wireOp",EDGE,"E10.33.2"),sQuery(id+"F0.wireOp",EDGE,"E10.33.3"),sQuery(id+"F0.wireOp",EDGE,"E10.33.4"),sQuery(id+"F0.wireOp",EDGE,"E10.33.5"),sQuery(id+"F0.wireOp",EDGE,"E10.34.0"),sQuery(id+"F0.wireOp",EDGE,"E10.34.1"),sQuery(id+"F0.wireOp",EDGE,"E10.34.2"),sQuery(id+"F0.wireOp",EDGE,"E10.34.3"),sQuery(id+"F0.wireOp",EDGE,"E10.34.4"),sQuery(id+"F0.wireOp",EDGE,"E10.34.5"),sQuery(id+"F0.wireOp",EDGE,"E11.trimOffspring"),sQuery(id+"F0.wireOp",EDGE,"E12.trimOffspring"),sQuery(id+"F0.wireOp",EDGE,"E13.trimOffspring"),sQuery(id+"F0.wireOp",EDGE,"E14.trimOffspring"),sQuery(id+"F0.wireOp",EDGE,"E15.trimOffspring"),sQuery(id+"F0.wireOp",EDGE,"E16.trimOffspring"),sQuery(id+"F0.wireOp",EDGE,"E17.trimOffspring"),sQuery(id+"F0.wireOp",EDGE,"E18.trimOffspring"),sQuery(id+"F0.wireOp",EDGE,"E19.trimOffspring"),sQuery(id+"F0.wireOp",EDGE,"E20.trimOffspring"),sQuery(id+"F0.wireOp",EDGE,"E21.trimOffspring"),sQuery(id+"F0.wireOp",EDGE,"E22.trimOffspring"),sQuery(id+"F0.wireOp",EDGE,"E23.trimOffspring"),sQuery(id+"F0.wireOp",EDGE,"E24.trimOffspring"),sQuery(id+"F0.wireOp",EDGE,"E25.trimOffspring"),sQuery(id+"F0.wireOp",EDGE,"E26.trimOffspring"),sQuery(id+"F0.wireOp",EDGE,"E27.trimOffspring"),sQuery(id+"F0.wireOp",EDGE,"E28.trimOffspring"),sQuery(id+"F0.wireOp",EDGE,"E29.trimOffspring"),sQuery(id+"F0.wireOp",EDGE,"E30.trimOffspring"),sQuery(id+"F0.wireOp",EDGE,"E31.trimOffspring"),sQuery(id+"F0.wireOp",EDGE,"E32.trimOffspring"),sQuery(id+"F0.wireOp",EDGE,"E33.trimOffspring"),sQuery(id+"F0.wireOp",EDGE,"E34.trimOffspring"),sQuery(id+"F0.wireOp",EDGE,"E35.trimOffspring"),sQuery(id+"F0.wireOp",EDGE,"E36.trimOffspring"),sQuery(id+"F0.wireOp",EDGE,"E37.trimOffspring"),sQuery(id+"F0.wireOp",EDGE,"E38.trimOffspring"),sQuery(id+"F0.wireOp",EDGE,"E39.trimOffspring"),sQuery(id+"F0.wireOp",EDGE,"E40.trimOffspring"),sQuery(id+"F0.wireOp",EDGE,"E41.trimOffspring"),sQuery(id+"F0.wireOp",EDGE,"E42.trimOffspring"),sQuery(id+"F0.wireOp",EDGE,"E43.trimOffspring"),sQuery(id+"F0.wireOp",EDGE,"E44.trimOffspring")])],"isStart":false});
            var sketch = newSketch(context, id + "F2", { "sketchPlane" : qUnion([Q0])});
            skCircle(sketch, "E45", {"center": v(0, 0) * mm, "radius": 11.43 * mm});
            skSolve(sketch);
        }
        {
            var Q0;
            Q0=makeQuery(id+"F2.imprint","IMPRINT",FACE,{"disambiguationData":[TD([[makeQuery(id+"F2.imprint","IMPRINT",EDGE,{"derivedFrom":sQuery(id+"F2.wireOp",EDGE,"E45")}),1.0]])]});
            extrude(context, id + "F3", {"entities" : qUnion([Q0]), "operationType" : NewBodyOperationType.ADD, "depth" : 7.37 * mm});
        }
        {
            var Q0;
            Q0=makeQuery(id+"F3.opExtrude","CAP_FACE",FACE,{"disambiguationData":[OSD([sQuery(id+"F2.wireOp",EDGE,"E45")])],"isStart":false});
            var sketch = newSketch(context, id + "F4", { "sketchPlane" : qUnion([Q0])});
            skLineSegment(sketch, "E46.0", {"start": v(-3.2, 5.6) * mm, "end": v(3.24, 5.58) * mm});
            skLineSegment(sketch, "E46.1", {"start": v(3.24, 5.58) * mm, "end": v(6.45, -0.02) * mm});
            skLineSegment(sketch, "E46.2", {"start": v(6.45, -0.02) * mm, "end": v(3.2, -5.6) * mm});
            skLineSegment(sketch, "E46.3", {"start": v(3.2, -5.6) * mm, "end": v(-3.24, -5.58) * mm});
            skLineSegment(sketch, "E46.4", {"start": v(-3.24, -5.58) * mm, "end": v(-6.45, 0.02) * mm});
            skLineSegment(sketch, "E46.5", {"start": v(-6.45, 0.02) * mm, "end": v(-3.2, 5.6) * mm});
            skSolve(sketch);
        }
        {
            var Q0;
            Q0=makeQuery(id+"F4.imprint","IMPRINT",FACE,{"disambiguationData":[TD([[makeQuery(id+"F4.imprint","IMPRINT",EDGE,{"derivedFrom":sQuery(id+"F4.wireOp",EDGE,"E46.0")}),-1.0]])]});
            extrude(context, id + "F5", {"entities" : qUnion([Q0]), "operationType" : NewBodyOperationType.REMOVE, "oppositeDirection" : true, "depth" : 50.8 * mm});
        }
    });
